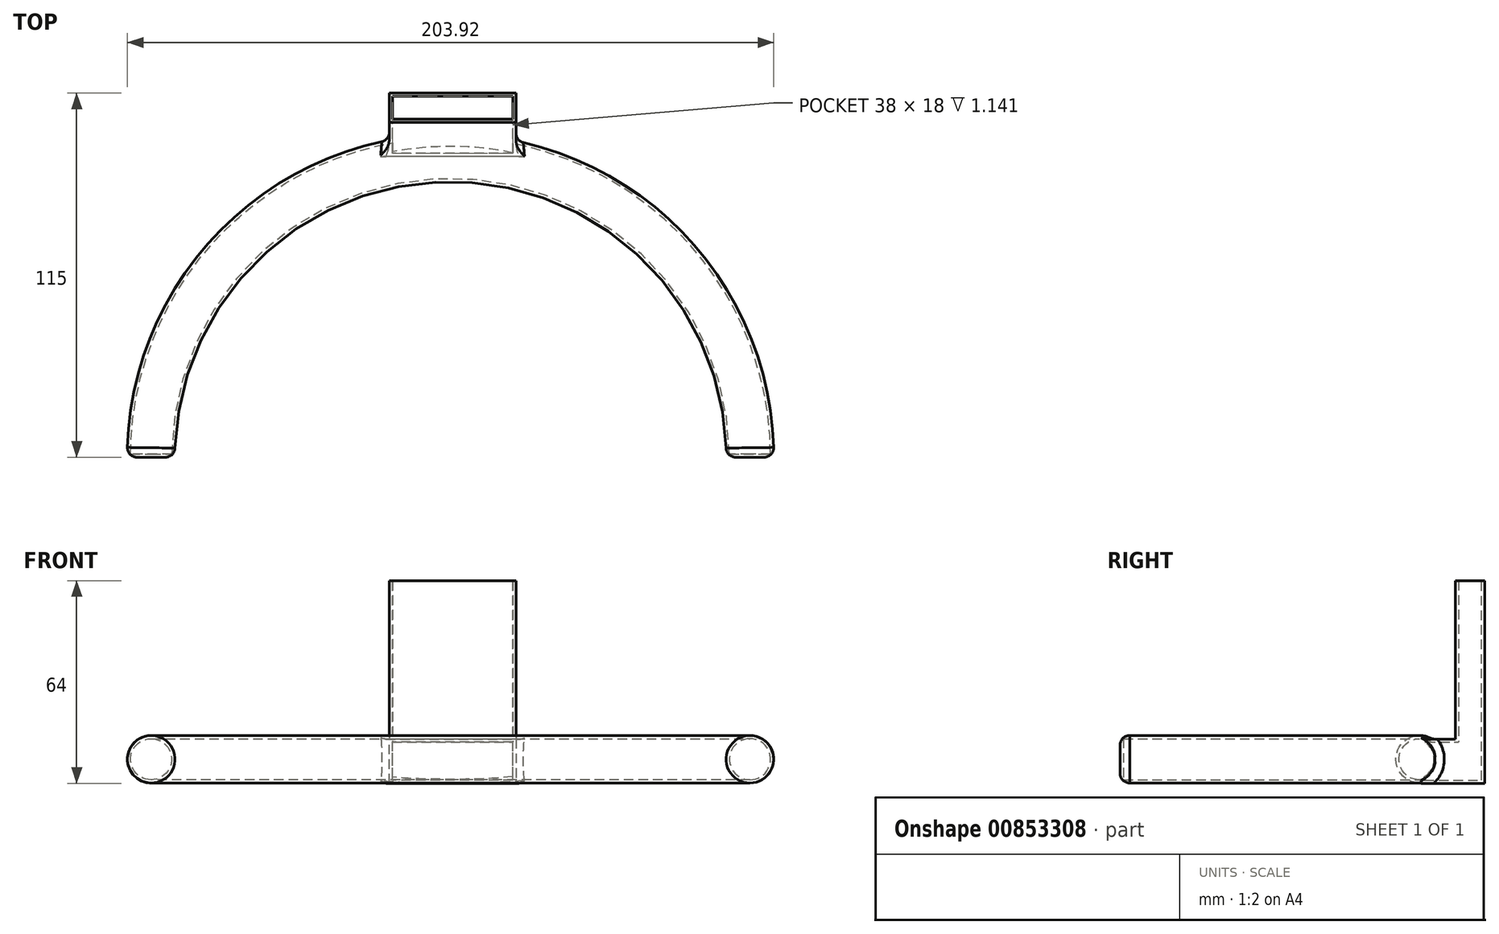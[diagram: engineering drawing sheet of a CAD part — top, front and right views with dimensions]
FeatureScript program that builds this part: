
annotation { "Feature Type Name" : "Feature", "Feature Type Description" : "" }
export const myFeature = defineFeature(function(context is Context, id is Id, definition is map)
    precondition{}
    {
        {
            var Q0;
            Q0=qCreatedBy(makeId("Top.planeOp"),FACE);
            var sketch = newSketch(context, id + "F0", { "sketchPlane" : qUnion([Q0])});
            skArc(sketch, "E0", {"start": v(75, 0) * mm, "mid": v(0, 75) * mm, "end": v(-75, 0) * mm});
            skPoint(sketch, "E1.start.orphan", {"position": v(-94.86, 0) * mm});
            skSolve(sketch);
        }
        {
            var Q0;
            Q0=qCreatedBy(makeId("Front.planeOp"),FACE);
            var sketch = newSketch(context, id + "F1", { "sketchPlane" : qUnion([Q0])});
            skCircle(sketch, "E2", {"center": v(-94.5, 0) * mm, "radius": 7.5 * mm});
            skSolve(sketch);
        }
        {
            var Q0;
            Q0=makeQuery(id+"F1.imprint","IMPRINT",FACE,{"disambiguationData":[TD([[makeQuery(id+"F1.imprint","IMPRINT",EDGE,{"derivedFrom":sQuery(id+"F1.wireOp",EDGE,"E2")}),1.0]])]});
            var Q1;
            Q1=sQuery(id+"F0.wireOp",EDGE,"E0");
            sweep(context, id + "F2", {"profiles" : qUnion([Q0]), "path" : qUnion([Q1])});
        }
        {
            var Q0;
            Q0=qCreatedBy(makeId("Front.planeOp"),FACE);
            cPlane(context, id + "F3", {"entities" : qUnion([Q0]), "cplaneType" : CPlaneType.OFFSET, "offset" : 115 * mm, "oppositeDirection" : true, "width" : 150 * mm, "height" : 150 * mm});
        }
        {
            var Q0;
            Q0=qCreatedBy(id+"F3.planeOp",FACE);
            var sketch = newSketch(context, id + "F4", { "sketchPlane" : qUnion([Q0])});
            skLineSegment(sketch, "E3.bottom", {"start": v(20.67, -7.62) * mm, "end": v(-19.33, -7.62) * mm});
            skLineSegment(sketch, "E3.top", {"start": v(20.67, 6.38) * mm, "end": v(-19.33, 6.38) * mm});
            skLineSegment(sketch, "E3.left", {"start": v(20.67, -7.62) * mm, "end": v(20.67, 6.38) * mm});
            skLineSegment(sketch, "E3.right", {"start": v(-19.33, -7.62) * mm, "end": v(-19.33, 6.38) * mm});
            skSolve(sketch);
        }
        {
            var Q0;
            Q0=makeQuery(id+"F4.imprint","IMPRINT",FACE,{"disambiguationData":[TD([[makeQuery(id+"F4.imprint","IMPRINT",EDGE,{"derivedFrom":sQuery(id+"F4.wireOp",EDGE,"E3.bottom")}),-1.0]])]});
            extrude(context, id + "F5", {"entities" : qUnion([Q0]), "operationType" : NewBodyOperationType.ADD, "depth" : 20 * mm, "offsetDistance" : 25 * mm});
        }
        {
            var Q0;
            Q0=makeQuery(id+"F5.opExtrude","SWEPT_FACE",FACE,{"disambiguationData":[OSD([sQuery(id+"F4.wireOp",EDGE,"E3.top")])]});
            var sketch = newSketch(context, id + "F6", { "sketchPlane" : qUnion([Q0])});
            skLineSegment(sketch, "E4.bottom", {"start": v(20.67, 115) * mm, "end": v(-19.33, 115) * mm});
            skLineSegment(sketch, "E4.top", {"start": v(20.67, 105.77) * mm, "end": v(-19.33, 105.77) * mm});
            skLineSegment(sketch, "E4.left", {"start": v(20.67, 115) * mm, "end": v(20.67, 105.77) * mm});
            skLineSegment(sketch, "E4.right", {"start": v(-19.33, 115) * mm, "end": v(-19.33, 105.77) * mm});
            skSolve(sketch);
        }
        {
            var Q0;
            Q0=makeQuery(id+"F6.imprint","IMPRINT",FACE,{"disambiguationData":[TD([[makeQuery(id+"F6.imprint","IMPRINT",EDGE,{"derivedFrom":sQuery(id+"F6.wireOp",EDGE,"E4.bottom")}),1.0]])]});
            extrude(context, id + "F7", {"entities" : qUnion([Q0]), "operationType" : NewBodyOperationType.ADD, "depth" : 50 * mm, "offsetDistance" : 25 * mm});
        }
        {
            var Q0;
            Q0=makeQuery(id+"F7.opExtrude","CAP_FACE",FACE,{"disambiguationData":[OSD([sQuery(id+"F6.wireOp",EDGE,"E4.bottom"),sQuery(id+"F6.wireOp",EDGE,"E4.top"),sQuery(id+"F6.wireOp",EDGE,"E4.left"),sQuery(id+"F6.wireOp",EDGE,"E4.right")])],"isStart":false});
            shell(context, id + "F8", {"entities" : qUnion([Q0]), "thickness" : 1 * mm});
        }
        {
            var Q0;
            Q0=makeQuery(id+"F7.opExtrude","CAP_EDGE",EDGE,{"disambiguationData":[OSD([sQuery(id+"F6.wireOp",EDGE,"E4.top")])],"isStart":true});
            var Q1;
            Q1=makeQuery(id+"F5.boolean.opBoolean","INTERSECT",EDGE,{"derivedFrom":[makeQuery(id+"F2.opSweep","SWEPT_FACE",FACE,{"disambiguationData":[OSD([sQuery(id+"F0.wireOp",EDGE,"E0"),sQuery(id+"F1.wireOp",EDGE,"E2")])]}),makeQuery(id+"F5.opExtrude","SWEPT_FACE",FACE,{"disambiguationData":[OSD([sQuery(id+"F4.wireOp",EDGE,"E3.left")])]})]});
            var Q2;
            Q2=makeQuery(id+"F5.boolean.opBoolean","INTERSECT",EDGE,{"derivedFrom":[makeQuery(id+"F2.opSweep","SWEPT_FACE",FACE,{"disambiguationData":[OSD([sQuery(id+"F0.wireOp",EDGE,"E0"),sQuery(id+"F1.wireOp",EDGE,"E2")])]}),makeQuery(id+"F5.opExtrude","SWEPT_FACE",FACE,{"disambiguationData":[OSD([sQuery(id+"F4.wireOp",EDGE,"E3.right")])]})]});
            var Q3;
            Q3=makeQuery(id+"F5.boolean.opBoolean","INTERSECT",EDGE,{"derivedFrom":[makeQuery(id+"F2.opSweep","SWEPT_FACE",FACE,{"disambiguationData":[OSD([sQuery(id+"F0.wireOp",EDGE,"E0"),sQuery(id+"F1.wireOp",EDGE,"E2")])]}),makeQuery(id+"F5.opExtrude","SWEPT_FACE",FACE,{"disambiguationData":[OSD([sQuery(id+"F4.wireOp",EDGE,"E3.top")])]})]});
            fillet(context, id + "F9", {"entities" : qUnion([Q0, Q1, Q2, Q3]), "radius" : 3 * mm, "tangentPropagation" : true, "allowEdgeOverflow" : false});
        }
        {
            var Q0;
            Q0=makeQuery(id+"F2.opSweep","CAP_FACE",FACE,{"disambiguationData":[OSD([sQuery(id+"F0.wireOp",VERTEX,"E0.start"),sQuery(id+"F1.wireOp",EDGE,"E2")])],"isStart":false});
            var Q1;
            Q1=makeQuery(id+"F2.opSweep","CAP_EDGE",EDGE,{"disambiguationData":[OSD([sQuery(id+"F0.wireOp",VERTEX,"E0.end"),sQuery(id+"F1.wireOp",EDGE,"E2")])],"isStart":true});
            fillet(context, id + "F10", {"entities" : qUnion([Q0, Q1]), "radius" : 3 * mm, "tangentPropagation" : true, "allowEdgeOverflow" : false});
        }
    });
